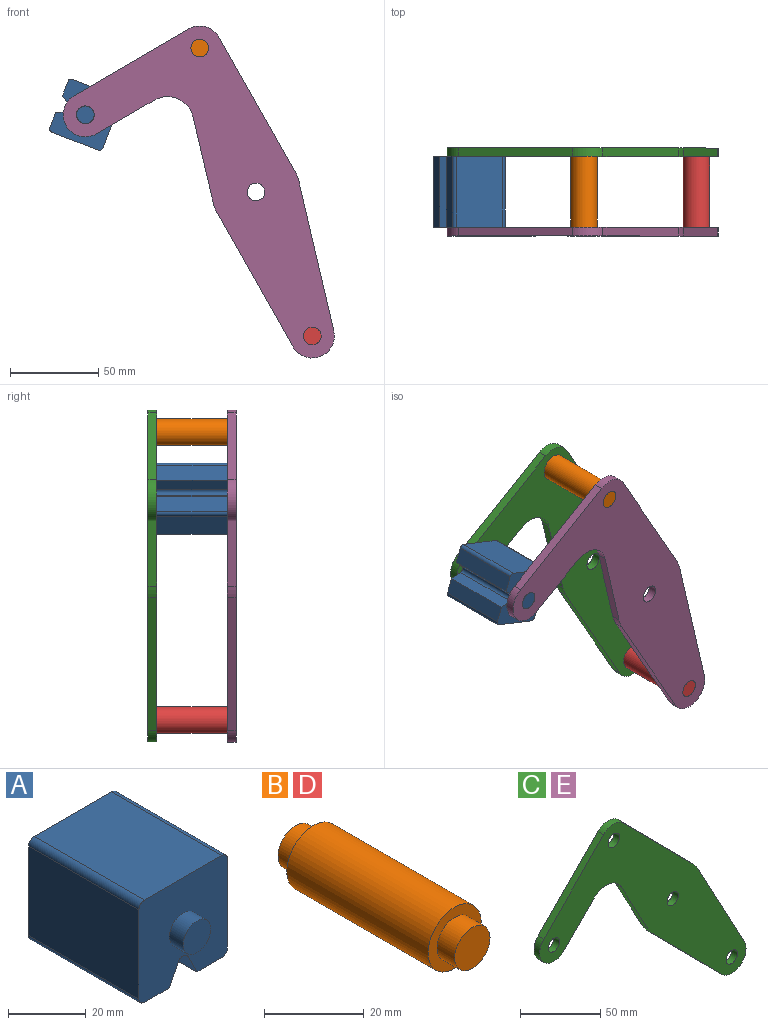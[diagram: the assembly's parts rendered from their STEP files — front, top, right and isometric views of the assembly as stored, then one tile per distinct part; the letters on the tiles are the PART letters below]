
ASSEMBLY  parts=5 mates=3
PART A: 18 faces, bbox 32.1x50x32.1 mm
  f0: plane 40x28.08mm, normal (1,0,0), area 1123.1mm2, adj f4,f10,f13,f14
  f1: plane 40x9.04mm, normal (0,0,-1), area 361.6mm2, adj f2,f4,f10,f14
  f2: plane 40x6.42mm, normal (-0.89,0,-0.45), area 287.2mm2, adj f1,f4,f10,f15
  f3: plane 40x6.42mm, normal (0.89,0,-0.45), area 287.2mm2, adj f4,f5,f10,f15
  f4: plane 32.08x32.08mm, normal (0,-1,0), area 900.6mm2, adj f0,f1,f2,f3,f5,f6,f7,f9
  f5: plane 40x9.04mm, normal (0,0,-1), area 361.6mm2, adj f3,f4,f10,f16
  f6: plane 40x28.08mm, normal (0,0,1), area 1123.1mm2, adj f4,f10,f13,f17
  f7: plane 40x28.08mm, normal (-1,0,0), area 1123.1mm2, adj f4,f10,f16,f17
  f8: plane 10x10mm, normal (0,-1,0), area 78.5mm2, adj f9
  f9: cylinder r=5mm len=10mm, axis (0,1,0), area 157.1mm2, adj f4,f8
  f10: plane 32.08x32.08mm, normal (0,1,0), area 900.6mm2, adj f0,f1,f2,f3,f5,f6,f7,f12
  f11: plane 10x10mm, normal (0,1,0), area 78.5mm2, adj f12
  f12: cylinder r=5mm len=10mm, axis (0,-1,0), area 157.1mm2, adj f10,f11
  f13: cylinder r=2mm len=40mm, axis (0,1,0), area 125.7mm2, adj f0,f4,f6,f10
  f14: cylinder r=2mm len=40mm, axis (0,-1,0), area 125.7mm2, adj f0,f1,f4,f10
  f15: cylinder r=2mm len=40mm, axis (0,1,0), area 177.1mm2, adj f2,f3,f4,f10
  f16: cylinder r=2mm len=40mm, axis (0,1,0), area 125.7mm2, adj f4,f5,f7,f10
  f17: cylinder r=2mm len=40mm, axis (0,-1,0), area 125.7mm2, adj f4,f6,f7,f10
PART B: 7 faces, bbox 15x50x15 mm
  f0: cylinder r=7.5mm len=40mm, axis (0,-1,0), area 1885mm2, adj f2,f5
  f1: cylinder r=5mm len=10mm, axis (0,1,0), area 157.1mm2, adj f2,f3
  f2: plane 15x15mm, normal (0,-1,0), area 98.2mm2, adj f0,f1
  f3: plane 10x10mm, normal (0,-1,0), area 78.5mm2, adj f1
  f4: cylinder r=5mm len=10mm, axis (0,-1,0), area 157.1mm2, adj f5,f6
  f5: plane 15x15mm, normal (0,1,0), area 98.2mm2, adj f0,f4
  f6: plane 10x10mm, normal (0,1,0), area 78.5mm2, adj f4
PART C: 18 faces, bbox 181.7x5x165.8 mm
  f0: plane 43.49x23.35mm, normal (-0.88,0,-0.47), area 246.8mm2, adj f1,f14,f16,f17
  f1: cylinder r=25mm len=5.75mm, axis (0,1,0), area 35.8mm2, adj f0,f2,f16,f17
  f2: plane 61.6x60.87mm, normal (-0.71,0,-0.7), area 433mm2, adj f1,f3,f16,f17
  f3: cylinder r=12.5mm len=21.39mm, axis (0,1,0), area 178.4mm2, adj f2,f4,f16,f17
  f4: plane 76.3x40.96mm, normal (0.88,0,0.47), area 433mm2, adj f3,f5,f16,f17
  f5: cylinder r=25mm len=5.75mm, axis (0,1,0), area 35.8mm2, adj f4,f6,f16,f17
  f6: plane 61.6x60.87mm, normal (0.71,0,0.7), area 433mm2, adj f5,f7,f16,f17
  f7: cylinder r=12.5mm len=17.78mm, axis (0,1,0), area 98.9mm2, adj f6,f8,f16,f17
  f8: plane 53.35x52.71mm, normal (-0.71,0,0.7), area 375mm2, adj f7,f9,f16,f17
  f9: cylinder r=12.5mm len=21.39mm, axis (0,1,0), area 196.3mm2, adj f8,f10,f16,f17
  f10: plane 26.86x26.54mm, normal (0.71,0,-0.7), area 188.8mm2, adj f9,f14,f16,f17
  f11: cylinder r=5mm len=10mm, axis (0,1,0), area 157.1mm2, adj f16,f17
  f12: cylinder r=5mm len=10mm, axis (0,1,0), area 157.1mm2, adj f16,f17
  f13: cylinder r=5mm len=10mm, axis (0,1,0), area 157.1mm2, adj f16,f17
  f14: cylinder r=15mm len=23.89mm, axis (0,1,0), area 140.2mm2, adj f0,f10,f16,f17
  f15: cylinder r=5mm len=10mm, axis (0,1,0), area 157.1mm2, adj f16,f17
  f16: plane 181.66x165.78mm, normal (0,-1,0), area 8710.1mm2, adj f0,f1,f2,f3,f4,f5,f6,f7
  f17: plane 181.66x165.78mm, normal (0,1,0), area 8710.1mm2, adj f0,f1,f2,f3,f4,f5,f6,f7
PART D: same geometry as B
PART E: same geometry as C
PLACE A rot(axis=(0,1,0),111.4deg) t=(-150.73,-20,-47.52)mm
PLACE B rot(axis=(0,1,0),15.1deg) t=(0,-20,0)mm
PLACE C rot(axis=(0,1,0),15.1deg) t=(0,25,0)mm
PLACE D rot(axis=(0,1,0),15.1deg) t=(63.69,-20,-163)mm
PLACE E rot(axis=(0,1,0),15.1deg) t=(0,-20,0)mm fixed
MATE fastened E.f3 <-> D.f0  axis (0,1,0) through (31.85,-20,-81.5)mm
MATE revolute A.f9 <-> E.f9  axis (0,1,0) through (-96.64,-20,43.72)mm
MATE fastened C.f7 <-> B.f0  axis (0,-1,0) through (-31.85,20,81.5)mm
